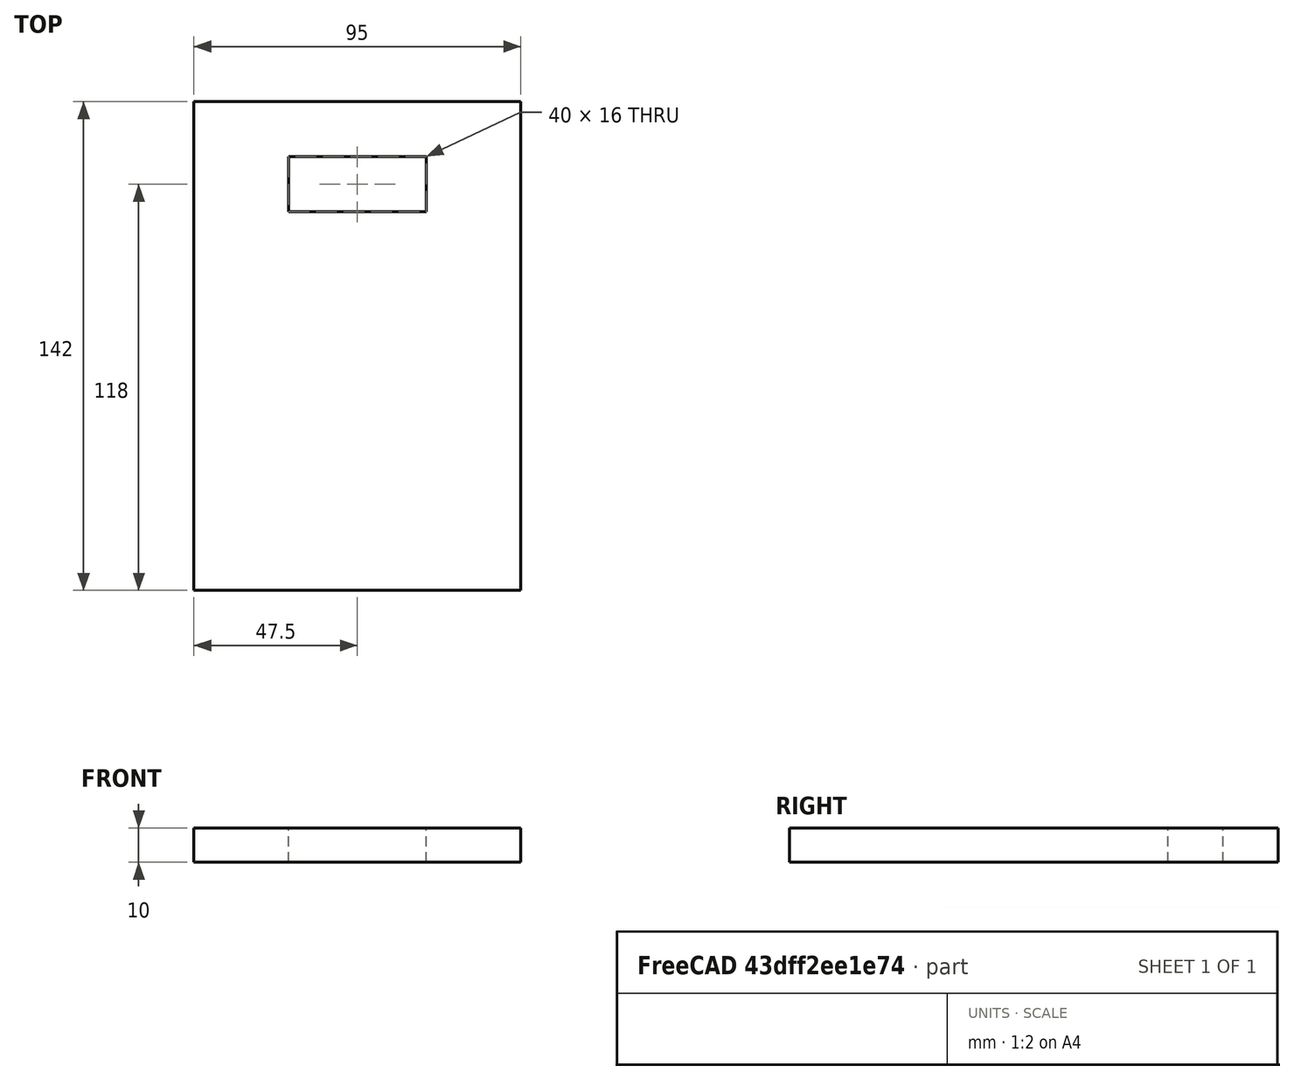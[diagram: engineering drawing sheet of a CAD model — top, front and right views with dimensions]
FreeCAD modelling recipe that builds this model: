
FCSTD DOCUMENT  (FreeCAD 0.15R4669 (Git))
Label: BR_supportMoteurTop
License: All rights reserved
LicenseURL: http://en.wikipedia.org/wiki/All_rights_reserved
objects: Sketcher::SketchObject×1, Part::Extrusion×1
note: 2 computed .brp shape members not serialized (recipe doc carries the construction recipe); baked Part::Feature solids carry a one-line shape summary decoded from their .brp

FEATURE [Sketcher::SketchObject] Sketch  label="sketchSupportMoteurTop"
  sketch-geometry (8):
    g0: LineSegment StartX=-47.5 StartY=0 StartZ=0 EndX=47.5 EndY=0 EndZ=0
    g1: LineSegment StartX=47.5 StartY=0 StartZ=0 EndX=47.5 EndY=-142 EndZ=0
    g2: LineSegment StartX=47.5 StartY=-142 StartZ=0 EndX=-47.5 EndY=-142 EndZ=0
    g3: LineSegment StartX=-47.5 StartY=-142 StartZ=0 EndX=-47.5 EndY=0 EndZ=0
    g4: LineSegment StartX=-20 StartY=-16 StartZ=0 EndX=20 EndY=-16 EndZ=0
    g5: LineSegment StartX=20 StartY=-16 StartZ=0 EndX=20 EndY=-32 EndZ=0
    g6: LineSegment StartX=20 StartY=-32 StartZ=0 EndX=-20 EndY=-32 EndZ=0
    g7: LineSegment StartX=-20 StartY=-32 StartZ=0 EndX=-20 EndY=-16 EndZ=0
  constraints (24):
    c: Coincident(g0,g1)
    c: Coincident(g1,g2)
    c: Coincident(g2,g3)
    c: Coincident(g3,g0)
    c: Horizontal(g0)
    c: Horizontal(g2)
    c: Vertical(g1)
    c: Vertical(g3)
    c: Symmetric(g0,g0,g-2)
    c: DistanceX(g0) = 95
    c: DistanceY(g3) = 142
    c: Coincident(g4,g5)
    c: Coincident(g5,g6)
    c: Coincident(g6,g7)
    c: Coincident(g7,g4)
    c: Horizontal(g4)
    c: Horizontal(g6)
    c: Vertical(g5)
    c: Vertical(g7)
    c: Symmetric(g6,g5,g-2)
    c: DistanceY(g5) = -16
    c: DistanceX(g4) = 40
    c: DistanceY(g4,g0) = 16
    c: PointOnObject(g0,g-1)
FEATURE [Part::Extrusion] Extrude  label="supportMoteurTop"
  Base = -> Sketch
  Dir = (0,0,10)
  Solid = true
